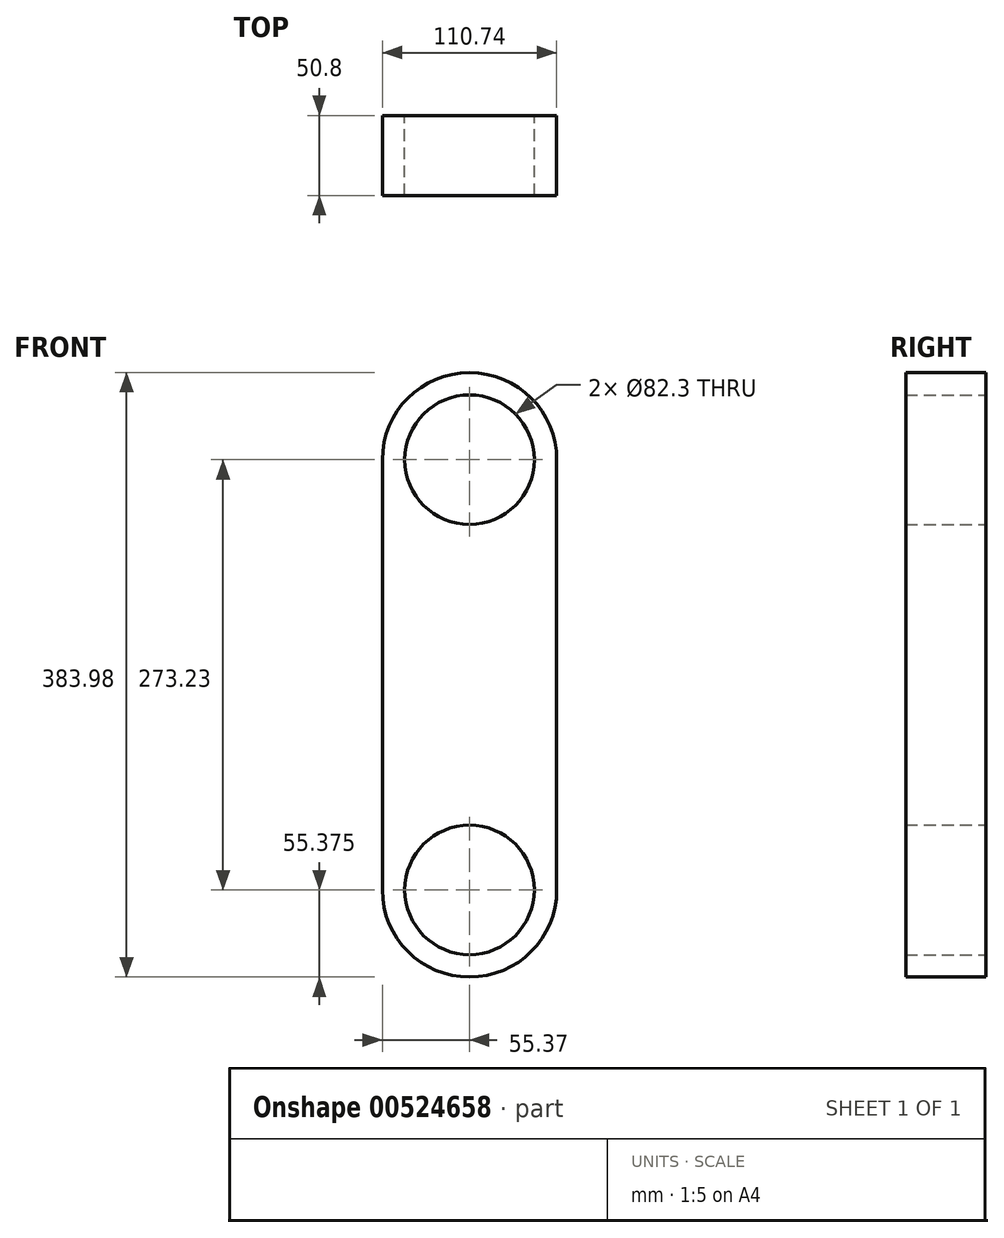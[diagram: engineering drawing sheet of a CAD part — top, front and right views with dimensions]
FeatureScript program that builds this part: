
annotation { "Feature Type Name" : "Feature", "Feature Type Description" : "" }
export const myFeature = defineFeature(function(context is Context, id is Id, definition is map)
    precondition{}
    {
        {
            var Q0;
            Q0=qCreatedBy(makeId("Front.planeOp"),FACE);
            var sketch = newSketch(context, id + "F0", { "sketchPlane" : qUnion([Q0])});
            skLineSegment(sketch, "E0.bottom", {"start": v(55.37, -136.61) * mm, "end": v(-55.37, -136.61) * mm});
            skLineSegment(sketch, "E0.top", {"start": v(55.37, 136.61) * mm, "end": v(-55.37, 136.61) * mm});
            skLineSegment(sketch, "E0.left", {"start": v(55.37, -136.61) * mm, "end": v(55.37, 136.61) * mm});
            skLineSegment(sketch, "E0.right", {"start": v(-55.37, -136.61) * mm, "end": v(-55.37, 136.61) * mm});
            skPoint(sketch, "E0.middle", {"position": v(0, 0) * mm});
            skCircle(sketch, "E1", {"center": v(0, 136.61) * mm, "radius": 55.37 * mm});
            skCircle(sketch, "E2", {"center": v(0, 136.61) * mm, "radius": 41.15 * mm});
            skCircle(sketch, "E3", {"center": v(0, -136.61) * mm, "radius": 55.37 * mm});
            skCircle(sketch, "E4", {"center": v(0, -136.61) * mm, "radius": 41.15 * mm});
            skSolve(sketch);
        }
        {
            var Q0;
            {var subQ1=sQuery(id+"F0.wireOp",EDGE,"E0.top");var subQ3=sQuery(id+"F0.wireOp",EDGE,"E2");var subQ4=makeQuery(id+"F0.imprint","INTERSECT",VERTEX,{"disambiguationData":[OD(0.0)],"derivedFrom":[subQ1,subQ3]});Q0=makeQuery(id+"F0.imprint","IMPRINT",FACE,{"disambiguationData":[TD([[makeQuery(id+"F0.imprint","IMPRINT",EDGE,{"disambiguationData":[TD([[subQ4,-1.0]])],"derivedFrom":subQ3}),-1.0]])]});}
            var Q1;
            {var subQ1=sQuery(id+"F0.wireOp",EDGE,"E0.top");var subQ3=sQuery(id+"F0.wireOp",EDGE,"E2");var subQ4=makeQuery(id+"F0.imprint","INTERSECT",VERTEX,{"disambiguationData":[OD(0.0)],"derivedFrom":[subQ1,subQ3]});Q1=makeQuery(id+"F0.imprint","IMPRINT",FACE,{"disambiguationData":[TD([[makeQuery(id+"F0.imprint","IMPRINT",EDGE,{"disambiguationData":[TD([[subQ4,1.0]])],"derivedFrom":subQ3}),-1.0]])]});}
            var Q2;
            {var subQ0=sQuery(id+"F0.wireOp",EDGE,"E0.left");Q2=makeQuery(id+"F0.imprint","IMPRINT",FACE,{"disambiguationData":[TD([[makeQuery(id+"F0.imprint","IMPRINT",EDGE,{"derivedFrom":subQ0}),1.0]])]});}
            var Q3;
            {var subQ0=sQuery(id+"F0.wireOp",EDGE,"E3");var subQ1=sQuery(id+"F0.wireOp",EDGE,"E0.bottom");var subQ2=makeQuery(id+"F0.imprint","INTERSECT",VERTEX,{"disambiguationData":[OD(0.0)],"derivedFrom":[subQ1,subQ0]});Q3=makeQuery(id+"F0.imprint","IMPRINT",FACE,{"disambiguationData":[TD([[makeQuery(id+"F0.imprint","IMPRINT",EDGE,{"disambiguationData":[TD([[subQ2,-1.0]])],"derivedFrom":subQ1}),-1.0]])]});}
            var Q4;
            {var subQ0=sQuery(id+"F0.wireOp",EDGE,"E3");var subQ1=sQuery(id+"F0.wireOp",EDGE,"E0.bottom");var subQ2=makeQuery(id+"F0.imprint","INTERSECT",VERTEX,{"disambiguationData":[OD(0.0)],"derivedFrom":[subQ1,subQ0]});Q4=makeQuery(id+"F0.imprint","IMPRINT",FACE,{"disambiguationData":[TD([[makeQuery(id+"F0.imprint","IMPRINT",EDGE,{"disambiguationData":[TD([[subQ2,-1.0]])],"derivedFrom":subQ1}),1.0]])]});}
            extrude(context, id + "F1", {"entities" : qUnion([Q0, Q1, Q2, Q3, Q4]), "depth" : 50.8 * mm, "offsetDistance" : 25.4 * mm});
        }
    });
